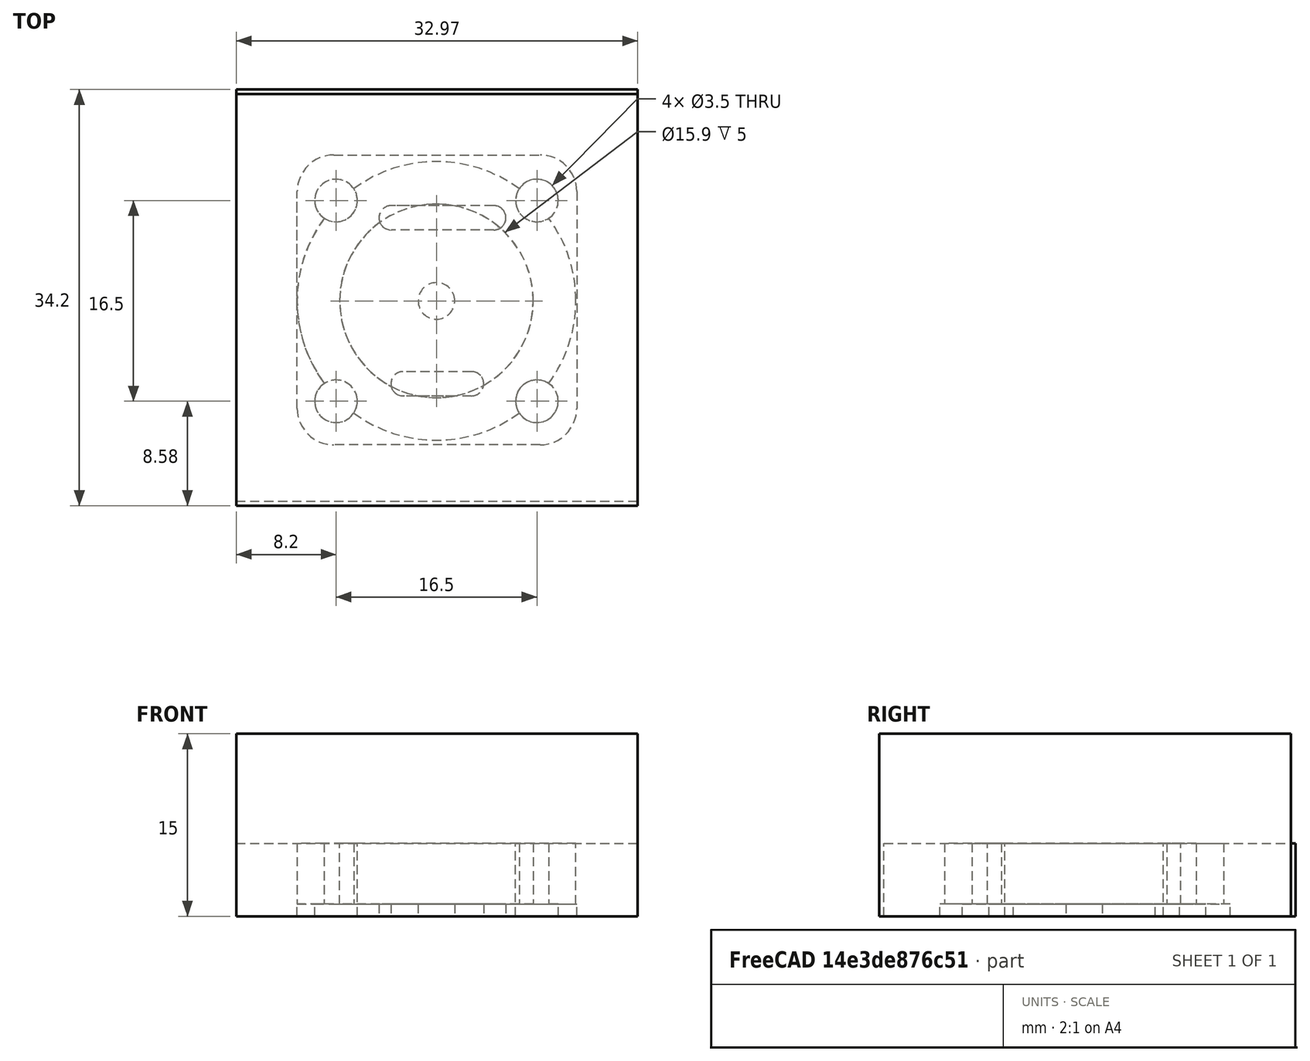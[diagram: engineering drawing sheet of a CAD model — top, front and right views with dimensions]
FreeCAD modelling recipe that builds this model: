
FCSTD DOCUMENT  (FreeCAD 0.18.4R)
Label: midi_pad_square_mount
License: All rights reserved
LicenseURL: http://en.wikipedia.org/wiki/All_rights_reserved
objects: Path::FeaturePython×16, Sketcher::SketchObject×7, Part::FeaturePython×6, App::MeasureDistance×4, App::FeaturePython×3, PartDesign::Pocket×3, App::DocumentObjectGroup×3, Path::FeatureCompoundPython×3, PartDesign::Pad×2, PartDesign::Hole×2, Mesh::FeaturePython×2, Spreadsheet::Sheet×1, Image::ImagePlane×1, PartDesign::Fillet×1, PartDesign::Body×1
note: 34 computed .brp shape members not serialized (recipe doc carries the construction recipe); baked Part::Feature solids carry a one-line shape summary decoded from their .brp

FEATURE [Sketcher::SketchObject] Sketch  label="base"
  MapMode = 5
  Support = -> [XY_Plane]
  sketch-geometry (4):
    g0: LineSegment StartX=-11.44 StartY=11.99 StartZ=0 EndX=11.52 EndY=11.99 EndZ=0
    g1: LineSegment StartX=11.52 StartY=11.99 StartZ=0 EndX=11.52 EndY=-11.83 EndZ=0
    g2: LineSegment StartX=11.52 StartY=-11.83 StartZ=0 EndX=-11.44 EndY=-11.83 EndZ=0
    g3: LineSegment StartX=-11.44 StartY=-11.83 StartZ=0 EndX=-11.44 EndY=11.99 EndZ=0
  constraints (12):
    c: Coincident(g0,g1)
    c: Coincident(g1,g2)
    c: Coincident(g2,g3)
    c: Coincident(g3,g0)
    c: Horizontal(g0)
    c: Horizontal(g2)
    c: Vertical(g1)
    c: Vertical(g3)
    c: DistanceY(g1,g1) = 23.82
    c: DistanceX(g0,g0) = 22.96
    c: Distance(g-1,g1) = 11.52
    c: Distance(g-1,g0) = 11.99
FEATURE [PartDesign::Pad] Pad  label="basePlate"
  Length = 1
  Length2 = 100
  Profile = -> Sketch
  Type = 0
  expr: Length = parameters.separator
FEATURE [Spreadsheet::Sheet] Spreadsheet  label="parameters"
  cells = A1=balero_R; B1(balero_R)=7.95; A2=balero_r; B2(balero_r)=2.35; A3=balero_h; B3(balero_h)=5; A4=pin_w; B4(pin_w)=10.2; A5=r_w; B5(r_w)=10; A6=cutout_d; B6(cutout_d)=1.7; A7=wall_thickness; B7(wall_thickness)=3.5; A8=separator; B8(separator)=1; A9=center hole D; B9(center_hole_D)=3; A10=screw Head D; B10(screwHeadD)=5.5; A11=screw D; B11(screwMountD)=3.5
FEATURE [App::FeaturePython] SetupSheet  # Path/CAM operation (typed FeaturePython)
  ClearanceHeightExpression = OpStockZMax+SetupSheet.ClearanceHeightOffset
  ClearanceHeightOffset = 5
  FinalDepthExpression = OpFinalDepth
  HorizRapid = 0
  SafeHeightExpression = OpStockZMax+SetupSheet.SafeHeightOffset
  SafeHeightOffset = 3
  StartDepthExpression = OpStartDepth
  StepDownExpression = OpToolDiameter
  VertRapid = 0
FEATURE [Path::FeaturePython] T2__Default_mill  label="mill standar"  # Path/CAM operation (typed FeaturePython)
  HorizFeed = 15
  HorizRapid = 0
  SpindleDir = 0
  SpindleSpeed = 12000
  ToolNumber = 1
  VertFeed = 15
  VertRapid = 0
  expr: HorizRapid = SetupSheet.HorizRapid
  expr: VertRapid = SetupSheet.VertRapid
FEATURE [Path::FeaturePython] Contour  # Path/CAM operation (typed FeaturePython)
  Active = true
  AreaParams:
    Tolerance = 1e-07
    FitArcs = True
    Simplify = False
    CleanDistance = 0.0
    Accuracy = 0.01
    Unit = 1.0
    MinArcPoints = 4
    MaxArcPoints = 100
    ClipperScale = 10000000.0
    Fill = 0
    Coplanar = 2
    Reorient = True
    Outline = False
    Explode = False
    OpenMode = 0
    Deflection = 0.01
    SubjectFill = 0
    ClipFill = 0
    Offset = 1.5
    ExtraPass = 0
    Stepover = 0.0
    LastStepover = 0.0
    JoinType = 0
    EndType = 0
    MiterLimit = 2.0
    RoundPrecision = 0.0
    PocketMode = 0
    ToolRadius = 1.0
    PocketExtraOffset = 0.0
    PocketStepover = 0.0
    PocketLastStepover = 0.0
    FromCenter = False
    Angle = 45.0
    AngleShift = 0.0
    Shift = 0.0
    Thicken = False
    SectionCount = -1
    Stepdown = 1.0
    SectionOffset = 0.0
    SectionTolerance = 1e-06
    SectionMode = 2
    Project = False
  ClearanceHeight = 12.7
  Direction = 0
  FinalDepth = 0
  JoinType = 0
  MiterLimit = 0.1
  OffsetExtra = 0
  OpFinalDepth = 0
  OpStartDepth = 7.7
  OpStockZMax = 7.7
  OpStockZMin = 0
  OpToolDiameter = 3
  PathParams = {'orientation': 1, 'feedrate': 15.0, 'feedrate_v': 15.0, 'verbose': True, 'resume_height': 10.7, 'retraction': 12.7, 'return_end': True, 'preamble': False}
  SafeHeight = 10.7
  Side = 0
  StartDepth = 7.7
  StartPoint = (0,0,0)
  StepDown = 0.6
  ToolController = -> T2__Default_mill
  UseComp = true
  UseStartPoint = false
  expr: ClearanceHeight = OpStockZMax + SetupSheet.ClearanceHeightOffset
  expr: SafeHeight = OpStockZMax + SetupSheet.SafeHeightOffset
  expr: StepDown = OpToolDiameter * 0.2
  expr: FinalDepth = OpFinalDepth
  expr: StartDepth = OpStartDepth
FEATURE [Path::FeaturePython] TagDressup  # Path/CAM operation (typed FeaturePython)
  Angle = 90
  Base = -> Contour
  Height = 2
  Positions = (6) [(-4.48226,-12.1484,0),(-12.7619,-2.19243,0),(-8.27966,9.95592,0),(3.92095,12.341,0),(12.5812,3.06393,0),(8.50562,-9.76359,0)]
  Radius = 0
  SegmentationFactor = 50
  Width = 2
FEATURE [Image::ImagePlane] ImagePlane
  Placement = pos=(99.4,-140.15,0) rot=(0,0,1;0rad)
  XSize = 222.326
  YSize = 305.698
FEATURE [App::MeasureDistance] Distance  label="Distance: left to center"
  Distance = 11.5
  P1 = (-11.5,0,0)
  P2 = (0,0,0)
FEATURE [App::MeasureDistance] Distance001  label="Distance: right to center"
  Distance = 11.5
  P1 = (11.5,0,0)
  P2 = (0,0,0)
FEATURE [App::MeasureDistance] Distance002  label="Distance: bottom to center"
  Distance = 7.58
  P1 = (0,-7.58,0)
  P2 = (0,0,0)
FEATURE [App::MeasureDistance] Distance003  label="Distance: up to center"
  Distance = 7.56
  P1 = (0,7.56,0)
  P2 = (0,0,0)
FEATURE [Sketcher::SketchObject] Sketch001  label="balero+wall"
  MapMode = 5
  Placement = pos=(0,0,1) rot=(0,0,1;0rad)
  Support = -> [Pad]
  expr: Constraints[1] = parameters.balero_R + parameters.wall_thickness
  sketch-geometry (1):
    g0: Circle CenterX=0 CenterY=0 CenterZ=0 NormalX=0 NormalY=0 NormalZ=1 AngleXU=0 Radius=11.45
  constraints (2):
    c: Coincident(g0,g-1)
    c: Radius(g0) = 11.45
FEATURE [PartDesign::Fillet] Fillet
  Base = -> Pad [Edge5,Edge8,Edge2,Edge1]
  BaseFeature = -> Pad
  Radius = 3
FEATURE [PartDesign::Pad] Pad001  label="baleroHolderVolume"
  BaseFeature = -> Fillet
  Length = 5
  Length2 = 100
  Profile = -> Sketch001
  Type = 0
  expr: Length = parameters.balero_h
FEATURE [Sketcher::SketchObject] Sketch002  label="baleroHolderInnerWall"
  MapMode = 5
  Placement = pos=(0,0,6) rot=(0,0,1;0rad)
  Support = -> [Pad001]
  expr: Constraints[1] = parameters.balero_R
  sketch-geometry (1):
    g0: Circle CenterX=0 CenterY=0 CenterZ=0 NormalX=0 NormalY=0 NormalZ=1 AngleXU=0 Radius=7.95
  constraints (2):
    c: Coincident(g0,g-1)
    c: Radius(g0) = 7.95
FEATURE [PartDesign::Pocket] Pocket  label="baleroHolderPocket"
  BaseFeature = -> Pad001
  Length = 5
  Length2 = 100
  Profile = -> Sketch002
  Type = 0
  expr: Length = parameters.balero_h
FEATURE [Sketcher::SketchObject] Sketch003  label="pin cutout shape"
  MapMode = 5
  Placement = pos=(0,0,0) rot=(1,0,0;3.14159rad)
  Support = -> [Pocket]
  sketch-geometry (8):
    g0: ArcOfCircle CenterX=4.7 CenterY=-6.83 CenterZ=0 NormalX=0 NormalY=0 NormalZ=1 AngleXU=0 Radius=1 StartAngle=4.71239 EndAngle=7.85398
    g1: ArcOfCircle CenterX=-3.72 CenterY=-6.83 CenterZ=0 NormalX=0 NormalY=0 NormalZ=1 AngleXU=0 Radius=1 StartAngle=1.5708 EndAngle=4.71239
    g2: LineSegment StartX=4.7 StartY=-5.83 StartZ=0 EndX=-3.72 EndY=-5.83 EndZ=0
    g3: LineSegment StartX=4.7 StartY=-7.83 StartZ=0 EndX=-3.72 EndY=-7.83 EndZ=0
    g4: ArcOfCircle CenterX=2.88 CenterY=6.81 CenterZ=0 NormalX=0 NormalY=0 NormalZ=1 AngleXU=0 Radius=1 StartAngle=4.71239 EndAngle=7.85398
    g5: ArcOfCircle CenterX=-2.74 CenterY=6.81 CenterZ=0 NormalX=0 NormalY=0 NormalZ=1 AngleXU=0 Radius=1 StartAngle=1.5708 EndAngle=4.71239
    g6: LineSegment StartX=2.88 StartY=7.81 StartZ=0 EndX=-2.74 EndY=7.81 EndZ=0
    g7: LineSegment StartX=2.88 StartY=5.81 StartZ=0 EndX=-2.74 EndY=5.81 EndZ=0
  constraints (20):
    c: Tangent(g0,g3) = 1.5708
    c: Tangent(g0,g2) = -1.5708
    c: Tangent(g2,g1) = -1.5708
    c: Tangent(g3,g1) = 1.5708
    c: Horizontal(g2)
    c: Equal(g0,g1)
    c: Tangent(g4,g7) = 1.5708
    c: Tangent(g4,g6) = -1.5708
    c: Tangent(g6,g5) = -1.5708
    c: Tangent(g7,g5) = 1.5708
    c: Horizontal(g6)
    c: Equal(g4,g5)
    c: Distance(g-1,g2) = 5.83
    c: Distance(g-1,g7) = 5.81
    c: Radius(g1) = 1
    c: Radius(g5) = 1
    c: DistanceX(g5,g-1) = 2.74
    c: DistanceX(g-1,g0) = 4.7
    c: DistanceX(g1,g-1) = 3.72
    c: DistanceX(g-1,g4) = 2.88
FEATURE [PartDesign::Pocket] Pocket001  label="pin cutout pocket"
  BaseFeature = -> Pocket
  Length = 1
  Length2 = 100
  Profile = -> Sketch003
  Type = 0
  expr: Length = parameters.separator
FEATURE [Sketcher::SketchObject] Sketch004  label="mount holes"
  MapMode = 5
  Placement = pos=(0,0,0) rot=(1,0,0;3.14159rad)
  Support = -> [Pocket001]
  sketch-geometry (4):
    g0: Circle CenterX=8.25 CenterY=8.25 CenterZ=0 NormalX=0 NormalY=0 NormalZ=1 AngleXU=0 Radius=1.75
    g1: Circle CenterX=-8.25 CenterY=8.25 CenterZ=0 NormalX=0 NormalY=0 NormalZ=1 AngleXU=0 Radius=1.75
    g2: Circle CenterX=8.25 CenterY=-8.25 CenterZ=0 NormalX=0 NormalY=0 NormalZ=1 AngleXU=0 Radius=1.75
    g3: Circle CenterX=-8.25 CenterY=-8.25 CenterZ=0 NormalX=0 NormalY=0 NormalZ=1 AngleXU=0 Radius=1.75
  constraints (12):
    c: DistanceY(g3,g-1) = 8.25
    c: DistanceY(g2,g-1) = 8.25
    c: DistanceY(g-1,g0) = 8.25
    c: DistanceY(g-1,g1) = 8.25
    c: DistanceX(g1,g-1) = 8.25
    c: DistanceX(g-1,g0) = 8.25
    c: DistanceX(g-1,g2) = 8.25
    c: DistanceX(g3,g-1) = 8.25
    c: Diameter(g1) = 3.5
    c: Equal(g1,g0)
    c: Equal(g1,g2)
    c: Equal(g1,g3)
FEATURE [PartDesign::Hole] Hole  label="mount Hole"
  BaseFeature = -> Pocket001
  Depth = 9
  DepthType = 0
  Diameter = 3.5
  DrillPoint = 0
  DrillPointAngle = 118
  HoleCutCountersinkAngle = 90
  HoleCutDepth = 0
  HoleCutDiameter = 0
  HoleCutType = 0
  ModelActualThread = false
  Profile = -> Sketch004
  Tapered = false
  TaperedAngle = 90
  ThreadAngle = 0
  ThreadClass = 0
  ThreadCutOffInner = 0
  ThreadCutOffOuter = 0
  ThreadDirection = 0
  ThreadFit = 0
  ThreadPitch = 0
  ThreadSize = 0
  ThreadType = 0
  Threaded = false
FEATURE [Sketcher::SketchObject] Sketch005  label="center hole"
  MapMode = 5
  Placement = pos=(0,0,6) rot=(0,0,1;0rad)
  Support = -> [Hole]
  expr: Constraints[1] = parameters.center_hole_D
  sketch-geometry (1):
    g0: Circle CenterX=0 CenterY=0 CenterZ=0 NormalX=0 NormalY=0 NormalZ=1 AngleXU=0 Radius=1.5
  constraints (2):
    c: Coincident(g0,g-1)
    c: Diameter(g0) = 3
FEATURE [PartDesign::Hole] Hole001  label="center hole cut"
  BaseFeature = -> Hole
  Depth = 25
  DepthType = 1
  Diameter = 3
  DrillPoint = 0
  DrillPointAngle = 118
  HoleCutCountersinkAngle = 90
  HoleCutDepth = 0
  HoleCutDiameter = 0
  HoleCutType = 0
  ModelActualThread = false
  Profile = -> Sketch005
  Tapered = false
  TaperedAngle = 90
  ThreadAngle = 0
  ThreadClass = 0
  ThreadCutOffInner = 0
  ThreadCutOffOuter = 0
  ThreadDirection = 0
  ThreadFit = 0
  ThreadPitch = 0
  ThreadSize = 0
  ThreadType = 0
  Threaded = false
FEATURE [Sketcher::SketchObject] Sketch006  label="screwHeadSpace"
  MapMode = 5
  Placement = pos=(0,0,6) rot=(0,0,1;0rad)
  Support = -> [Hole001]
  expr: Constraints[8] = parameters.screwHeadD
  sketch-geometry (4):
    g0: Circle CenterX=-8.25 CenterY=8.25 CenterZ=0 NormalX=0 NormalY=0 NormalZ=1 AngleXU=0 Radius=2.75
    g1: Circle CenterX=-8.25 CenterY=-8.25 CenterZ=0 NormalX=0 NormalY=0 NormalZ=1 AngleXU=0 Radius=2.75
    g2: Circle CenterX=8.25 CenterY=-8.25 CenterZ=0 NormalX=0 NormalY=0 NormalZ=1 AngleXU=0 Radius=2.75
    g3: Circle CenterX=8.25 CenterY=8.25 CenterZ=0 NormalX=0 NormalY=0 NormalZ=1 AngleXU=0 Radius=2.75
  constraints (12):
    c: DistanceX(g0,g-1) = 8.25
    c: DistanceX(g-1,g3) = 8.25
    c: DistanceX(g-1,g2) = 8.25
    c: DistanceX(g1,g-1) = 8.25
    c: DistanceY(g-1,g0) = 8.25
    c: DistanceY(g-1,g3) = 8.25
    c: DistanceY(g2,g-1) = 8.25
    c: DistanceY(g1,g-1) = 8.25
    c: Diameter(g0) = 5.5
    c: Equal(g0,g3)
    c: Equal(g0,g2)
    c: Equal(g0,g1)
FEATURE [App::FeaturePython] SetupSheet001  # Path/CAM operation (typed FeaturePython)
  ClearanceHeightExpression = OpStockZMax+SetupSheet001.ClearanceHeightOffset
  ClearanceHeightOffset = 5
  FinalDepthExpression = OpFinalDepth
  HorizRapid = 0
  SafeHeightExpression = OpStockZMax+SetupSheet001.SafeHeightOffset
  SafeHeightOffset = 3
  StartDepthExpression = OpStartDepth
  StepDownExpression = OpToolDiameter
  VertRapid = 0
FEATURE [Path::FeaturePython] T2__Mill_Bit_standard  label="T2: Mill Bit standard"  # Path/CAM operation (typed FeaturePython)
  HorizFeed = 15
  HorizRapid = 0
  SpindleDir = 0
  SpindleSpeed = 12000
  ToolNumber = 1
  VertFeed = 15
  VertRapid = 0
  expr: HorizRapid = SetupSheet001.HorizRapid
  expr: VertRapid = SetupSheet001.VertRapid
FEATURE [Path::FeaturePython] Contour001  label="mill contour"  # Path/CAM operation (typed FeaturePython)
  Active = true
  AreaParams:
    Tolerance = 1e-07
    FitArcs = True
    Simplify = False
    CleanDistance = 0.0
    Accuracy = 0.01
    Unit = 1.0
    MinArcPoints = 4
    MaxArcPoints = 100
    ClipperScale = 10000000.0
    Fill = 0
    Coplanar = 2
    Reorient = True
    Outline = False
    Explode = False
    OpenMode = 0
    Deflection = 0.01
    SubjectFill = 0
    ClipFill = 0
    Offset = 1.55
    ExtraPass = 0
    Stepover = 0.0
    LastStepover = 0.0
    JoinType = 0
    EndType = 0
    MiterLimit = 2.0
    RoundPrecision = 0.0
    PocketMode = 0
    ToolRadius = 1.0
    PocketExtraOffset = 0.0
    PocketStepover = 0.0
    PocketLastStepover = 0.0
    FromCenter = False
    Angle = 45.0
    AngleShift = 0.0
    Shift = 0.0
    Thicken = False
    SectionCount = -1
    Stepdown = 1.0
    SectionOffset = 0.0
    SectionTolerance = 1e-06
    SectionMode = 2
    Project = False
  ClearanceHeight = 20
  Direction = 0
  FinalDepth = 0
  JoinType = 0
  MiterLimit = 0.1
  OffsetExtra = 0
  OpFinalDepth = 0
  OpStartDepth = 15
  OpStockZMax = 15
  OpStockZMin = 0
  OpToolDiameter = 3.1
  PathParams = {'orientation': 1, 'feedrate': 15.0, 'feedrate_v': 15.0, 'verbose': True, 'resume_height': 18.0, 'retraction': 20.0, 'return_end': True, 'preamble': False}
  SafeHeight = 18
  Side = 0
  StartDepth = 15
  StartPoint = (0,0,0)
  StepDown = 3.1
  ToolController = -> T2__Mill_Bit_standard
  UseComp = true
  UseStartPoint = false
  expr: ClearanceHeight = OpStockZMax + SetupSheet001.ClearanceHeightOffset
  expr: SafeHeight = OpStockZMax + SetupSheet001.SafeHeightOffset
  expr: StepDown = OpToolDiameter
  expr: FinalDepth = OpFinalDepth
  expr: StartDepth = OpStartDepth
FEATURE [App::FeaturePython] SetupSheet002  # Path/CAM operation (typed FeaturePython)
  ClearanceHeightExpression = OpStockZMax+SetupSheet002.ClearanceHeightOffset
  ClearanceHeightOffset = 5
  FinalDepthExpression = OpFinalDepth
  HorizRapid = 0
  SafeHeightExpression = OpStockZMax+SetupSheet002.SafeHeightOffset
  SafeHeightOffset = 3
  StartDepthExpression = OpStartDepth
  StepDownExpression = OpToolDiameter
  VertRapid = 0
FEATURE [Path::FeaturePython] T2__Mill_Bit_standard001  label="T2: Mill Bit standard001"  # Path/CAM operation (typed FeaturePython)
  HorizFeed = 0
  HorizRapid = 0
  SpindleDir = 0
  SpindleSpeed = 0
  ToolNumber = 2
  VertFeed = 0
  VertRapid = 0
  expr: HorizRapid = SetupSheet002.HorizRapid
  expr: VertRapid = SetupSheet002.VertRapid
FEATURE [Path::FeaturePython] Pocket_3D002  label="mill overall height"  # Path/CAM operation (typed FeaturePython)
  Active = true
  AreaParams:
    Tolerance = 1e-07
    FitArcs = True
    Simplify = False
    CleanDistance = 0.0
    Accuracy = 0.01
    Unit = 1.0
    MinArcPoints = 4
    MaxArcPoints = 100
    ClipperScale = 10000000.0
    Fill = 0
    Coplanar = 0
    Reorient = True
    Outline = False
    Explode = False
    OpenMode = 0
    Deflection = 0.01
    SubjectFill = 0
    ClipFill = 0
    Offset = 0.0
    ExtraPass = 0
    Stepover = 0.0
    LastStepover = 0.0
    JoinType = 0
    EndType = 0
    MiterLimit = 2.0
    RoundPrecision = 0.0
    PocketMode = 4
    ToolRadius = 1.55
    PocketExtraOffset = 0.0
    PocketStepover = 1.55
    PocketLastStepover = 0.0
    FromCenter = True
    Angle = 45.0
    AngleShift = 0.0
    Shift = 0.0
    Thicken = False
    SectionCount = -1
    Stepdown = 1.0
    SectionOffset = 0.0
    SectionTolerance = 1e-06
    SectionMode = 2
    Project = False
  ClearanceHeight = 20
  CutMode = 0
  ExtraOffset = 0
  FinalDepth = 6
  FinishDepth = 0
  KeepToolDown = false
  MinTravel = false
  OffsetPattern = 3
  OpFinalDepth = 6
  OpStartDepth = 15
  OpStockZMax = 15
  OpStockZMin = 0
  OpToolDiameter = 3.1
  PathParams = {'orientation': 1, 'feedrate': 15.0, 'feedrate_v': 15.0, 'verbose': True, 'resume_height': 18.0, 'retraction': 20.0, 'return_end': True, 'preamble': False}
  SafeHeight = 18
  StartAt = 0
  StartDepth = 15
  StartPoint = (0,0,0)
  StepDown = 3.1
  StepOver = 50
  ToolController = -> T2__Mill_Bit_standard
  UseStartPoint = false
  ZigZagAngle = 45
  expr: ClearanceHeight = OpStockZMax + SetupSheet001.ClearanceHeightOffset
  expr: SafeHeight = OpStockZMax + SetupSheet001.SafeHeightOffset
  expr: StepDown = OpToolDiameter
  expr: FinalDepth = OpFinalDepth
  expr: StartDepth = OpStartDepth
FEATURE [Path::FeaturePython] TagDressup001  label="tagged contour"  # Path/CAM operation (typed FeaturePython)
  Angle = 45
  Base = -> Contour001
  Height = 1.5
  Positions = (4) [(13.0676,0.140806,0),(0.100806,-13.3776,0),(-13.0109,-4.22495,0),(-0.0208058,13.5376,0)]
  Radius = 0
  SegmentationFactor = 50
  Width = 8.79
FEATURE [Mesh::FeaturePython] CutMaterial  # WARN: FeaturePython — macro-defined, semantics opaque (R4)
FEATURE [Mesh::FeaturePython] CutMaterial001  # WARN: FeaturePython — macro-defined, semantics opaque (R4)
FEATURE [PartDesign::Pocket] Pocket002  label="screwHeadPocket"
  BaseFeature = -> Hole001
  Length = 5
  Length2 = 100
  Profile = -> Sketch006
  Type = 0
  expr: Length = parameters.balero_h
FEATURE [PartDesign::Body] Body
  Group = -> [Sketch,Pad,Fillet,Pad001,Sketch002,Pocket,Sketch003,Pocket001,Sketch004,Hole,Sketch005,Hole001,Sketch006,Pocket002]
  Origin = -> Origin
  Tip = -> Pocket002
FEATURE [Part::FeaturePython] Clone  label="Model-Body"  # Draft clone (typed FeaturePython)
  AttacherType = Attacher::AttachEngine3D
  Fuse = false
  Objects = -> [Body]
  PathResource = Model
  Scale = (1,1,1)
FEATURE [App::DocumentObjectGroup] Model
  Group = -> [Clone]
FEATURE [Part::FeaturePython] Stock001  label="Stock acrylic"  # WARN: FeaturePython — macro-defined, semantics opaque (R4)
  Base = -> Model
  ExtXneg = 5
  ExtXpos = 5
  ExtYneg = 5
  ExtYpos = 5
  ExtZneg = 0
  ExtZpos = 0
  Placement = pos=(-11.45,-11.45,0) rot=(0,0,1;0rad)
  StockType = FromBase
FEATURE [Path::FeaturePython] Pocket_3D  label="Balero_Pocket_3D"  # Path/CAM operation (typed FeaturePython)
  Active = true
  AreaParams:
    Tolerance = 1e-07
    FitArcs = True
    Simplify = False
    CleanDistance = 0.0
    Accuracy = 0.01
    Unit = 1.0
    MinArcPoints = 4
    MaxArcPoints = 100
    ClipperScale = 10000000.0
    Fill = 0
    Coplanar = 0
    Reorient = True
    Outline = False
    Explode = False
    OpenMode = 0
    Deflection = 0.01
    SubjectFill = 0
    ClipFill = 0
    Offset = 0.0
    ExtraPass = 0
    Stepover = 0.0
    LastStepover = 0.0
    JoinType = 0
    EndType = 0
    MiterLimit = 2.0
    RoundPrecision = 0.0
    PocketMode = 4
    ToolRadius = 1.5
    PocketExtraOffset = 0.0
    PocketStepover = 0.6000000000000001
    PocketLastStepover = 0.0
    FromCenter = True
    Angle = 45.0
    AngleShift = 0.0
    Shift = 0.0
    Thicken = False
    SectionCount = -1
    Stepdown = 1.0
    SectionOffset = 0.0
    SectionTolerance = 1e-06
    SectionMode = 2
    Project = False
  Base = -> [Clone]
  ClearanceHeight = 11
  CutMode = 0
  ExtraOffset = 0
  FinalDepth = 0
  FinishDepth = 0
  KeepToolDown = false
  MinTravel = false
  OffsetPattern = 3
  OpFinalDepth = 0
  OpStartDepth = 6
  OpStockZMax = 6
  OpStockZMin = 0
  OpToolDiameter = 3
  PathParams = {'orientation': 1, 'feedrate': 15.0, 'feedrate_v': 15.0, 'verbose': True, 'resume_height': 9.0, 'retraction': 11.0, 'return_end': True, 'preamble': False}
  SafeHeight = 9
  StartAt = 0
  StartDepth = 6
  StartPoint = (0,0,0)
  StepDown = 0.6
  StepOver = 20
  ToolController = -> T2__Default_mill
  UseStartPoint = false
  ZigZagAngle = 45
  expr: ClearanceHeight = OpStockZMax + SetupSheet.ClearanceHeightOffset
  expr: SafeHeight = OpStockZMax + SetupSheet.SafeHeightOffset
  expr: StepDown = OpToolDiameter * 0.2
  expr: FinalDepth = OpFinalDepth
  expr: StartDepth = OpStartDepth
FEATURE [Path::FeatureCompoundPython] Operations  # Path/CAM operation (typed FeaturePython)
  Group = -> [Pocket_3D,TagDressup]
  UsePlacements = false
FEATURE [Path::FeaturePython] Job  # Path/CAM operation (typed FeaturePython)
  GeometryTolerance = 0.01
  Model = -> Model
  Operations = -> Operations
  PostProcessor = 5
  SetupSheet = -> SetupSheet
  Stock = -> Stock001
  ToolController = -> [T2__Default_mill]
FEATURE [Part::FeaturePython] Clone001  label="Model-Body001"  # Draft clone (typed FeaturePython)
  AttacherType = Attacher::AttachEngine3D
  Fuse = false
  Objects = -> [Body]
  PathResource = Model
  Scale = (1,1,1)
FEATURE [App::DocumentObjectGroup] Model001
  Group = -> [Clone001]
FEATURE [Part::FeaturePython] Stock  # WARN: FeaturePython — macro-defined, semantics opaque (R4)
  Base = -> Model001
  ExtXneg = 5
  ExtXpos = 5
  ExtYneg = 5
  ExtYpos = 5
  ExtZneg = 0
  ExtZpos = 9
  Placement = pos=(-11.4489,-11.83,0) rot=(0,0,1;0rad)
  StockType = FromBase
FEATURE [Path::FeaturePython] Pocket_3D001  label="balero pocket"  # Path/CAM operation (typed FeaturePython)
  Active = true
  AreaParams:
    Tolerance = 1e-07
    FitArcs = True
    Simplify = False
    CleanDistance = 0.0
    Accuracy = 0.01
    Unit = 1.0
    MinArcPoints = 4
    MaxArcPoints = 100
    ClipperScale = 10000000.0
    Fill = 0
    Coplanar = 0
    Reorient = True
    Outline = False
    Explode = False
    OpenMode = 0
    Deflection = 0.01
    SubjectFill = 0
    ClipFill = 0
    Offset = 0.0
    ExtraPass = 0
    Stepover = 0.0
    LastStepover = 0.0
    JoinType = 0
    EndType = 0
    MiterLimit = 2.0
    RoundPrecision = 0.0
    PocketMode = 4
    ToolRadius = 1.55
    PocketExtraOffset = 0.0
    PocketStepover = 2.4800000000000004
    PocketLastStepover = 0.0
    FromCenter = True
    Angle = 45.0
    AngleShift = 0.0
    Shift = 0.0
    Thicken = False
    SectionCount = -1
    Stepdown = 1.0
    SectionOffset = 0.0
    SectionTolerance = 1e-06
    SectionMode = 2
    Project = False
  Base = -> [Clone001]
  ClearanceHeight = 20
  CutMode = 0
  ExtraOffset = 0
  FinalDepth = 1
  FinishDepth = 0
  KeepToolDown = false
  MinTravel = false
  OffsetPattern = 3
  OpFinalDepth = 1
  OpStartDepth = 15
  OpStockZMax = 15
  OpStockZMin = 0
  OpToolDiameter = 3.1
  PathParams = {'orientation': 1, 'feedrate': 15.0, 'feedrate_v': 15.0, 'verbose': True, 'resume_height': 18.0, 'retraction': 20.0, 'return_end': True, 'preamble': False}
  SafeHeight = 18
  StartAt = 0
  StartDepth = 15
  StartPoint = (0,0,0)
  StepDown = 3.1
  StepOver = 80
  ToolController = -> T2__Mill_Bit_standard
  UseStartPoint = false
  ZigZagAngle = 45
  expr: ClearanceHeight = OpStockZMax + SetupSheet001.ClearanceHeightOffset
  expr: SafeHeight = OpStockZMax + SetupSheet001.SafeHeightOffset
  expr: StepDown = OpToolDiameter
  expr: FinalDepth = OpFinalDepth
  expr: StartDepth = OpStartDepth
FEATURE [Part::FeaturePython] Clone002  label="Model-Body002"  # Draft clone (typed FeaturePython)
  AttacherType = Attacher::AttachEngine3D
  Fuse = false
  Objects = -> [Body]
  PathResource = Model
  Scale = (1,1,1)
FEATURE [App::DocumentObjectGroup] Model002
  Group = -> [Clone002]
FEATURE [Part::FeaturePython] Stock002  # WARN: FeaturePython — macro-defined, semantics opaque (R4)
  Base = -> Model002
  ExtXneg = 5
  ExtXpos = 5
  ExtYneg = 5
  ExtYpos = 5
  ExtZneg = 0
  ExtZpos = 9
  Placement = pos=(-11.45,-11.83,0) rot=(0,0,1;0rad)
  StockType = FromBase
FEATURE [Path::FeaturePython] Drilling  # Path/CAM operation (typed FeaturePython)
  Active = true
  AddTipLength = false
  Base = -> [Clone002]
  ClearanceHeight = 20
  DwellEnabled = false
  DwellTime = 0
  FinalDepth = 1
  OpFinalDepth = 1
  OpStartDepth = 15
  OpStockZMax = 15
  OpStockZMin = 0
  OpToolDiameter = 3.1
  PeckDepth = 1
  PeckEnabled = true
  RetractHeight = 10
  ReturnLevel = 0
  SafeHeight = 18
  StartDepth = 15
  ToolController = -> T2__Mill_Bit_standard001
  expr: ClearanceHeight = OpStockZMax + SetupSheet002.ClearanceHeightOffset
  expr: SafeHeight = OpStockZMax + SetupSheet002.SafeHeightOffset
  expr: FinalDepth = OpFinalDepth
  expr: StartDepth = OpStartDepth
FEATURE [Path::FeatureCompoundPython] Operations002  # Path/CAM operation (typed FeaturePython)
  Group = -> [Drilling]
  UsePlacements = false
FEATURE [Path::FeaturePython] Job002  # Path/CAM operation (typed FeaturePython)
  GeometryTolerance = 0.01
  Model = -> Model002
  Operations = -> Operations002
  PostProcessor = 5
  SetupSheet = -> SetupSheet002
  Stock = -> Stock002
  ToolController = -> [T2__Mill_Bit_standard001]
FEATURE [Path::FeaturePython] Drilling001  label="drill mounting holes"  # Path/CAM operation (typed FeaturePython)
  Active = true
  AddTipLength = false
  Base = -> [Clone001]
  ClearanceHeight = 20
  DwellEnabled = false
  DwellTime = 0
  FinalDepth = 0
  OpFinalDepth = 0
  OpStartDepth = 15
  OpStockZMax = 15
  OpStockZMin = 0
  OpToolDiameter = 3.1
  PeckDepth = 0
  PeckEnabled = true
  RetractHeight = 10
  ReturnLevel = 0
  SafeHeight = 18
  StartDepth = 15
  ToolController = -> T2__Mill_Bit_standard
  expr: ClearanceHeight = OpStockZMax + SetupSheet001.ClearanceHeightOffset
  expr: SafeHeight = OpStockZMax + SetupSheet001.SafeHeightOffset
  expr: FinalDepth = OpFinalDepth
  expr: StartDepth = OpStartDepth
FEATURE [Path::FeaturePython] Drilling002  label="drill center hole"  # Path/CAM operation (typed FeaturePython)
  Active = true
  AddTipLength = false
  Base = -> [Clone001]
  ClearanceHeight = 20
  DwellEnabled = false
  DwellTime = 0
  FinalDepth = 0
  OpFinalDepth = 0
  OpStartDepth = 15
  OpStockZMax = 15
  OpStockZMin = 0
  OpToolDiameter = 3.1
  PeckDepth = 1
  PeckEnabled = true
  RetractHeight = 10
  ReturnLevel = 0
  SafeHeight = 18
  StartDepth = 15
  ToolController = -> T2__Mill_Bit_standard
  expr: ClearanceHeight = OpStockZMax + SetupSheet001.ClearanceHeightOffset
  expr: SafeHeight = OpStockZMax + SetupSheet001.SafeHeightOffset
  expr: FinalDepth = OpFinalDepth
  expr: StartDepth = OpStartDepth
FEATURE [Path::FeatureCompoundPython] Operations001  # Path/CAM operation (typed FeaturePython)
  Group = -> [Pocket_3D002,Drilling002,Pocket_3D001,TagDressup001,Drilling001]
  UsePlacements = false
FEATURE [Path::FeaturePython] Job001  label="UpperSideFoamTest"  # Path/CAM operation (typed FeaturePython)
  Description = Testing the Gcode of the Upper side of the piece cut on foam
  GeometryTolerance = 0.01
  Model = -> Model001
  Operations = -> Operations001
  PostProcessor = 4
  PostProcessorOutputFile = <userpath>/FreeCAD/Projects/midi_pad/midi_pad_AS5600_mount_on_foam.gcode
  SetupSheet = -> SetupSheet001
  Stock = -> Stock
  ToolController = -> [T2__Mill_Bit_standard]
